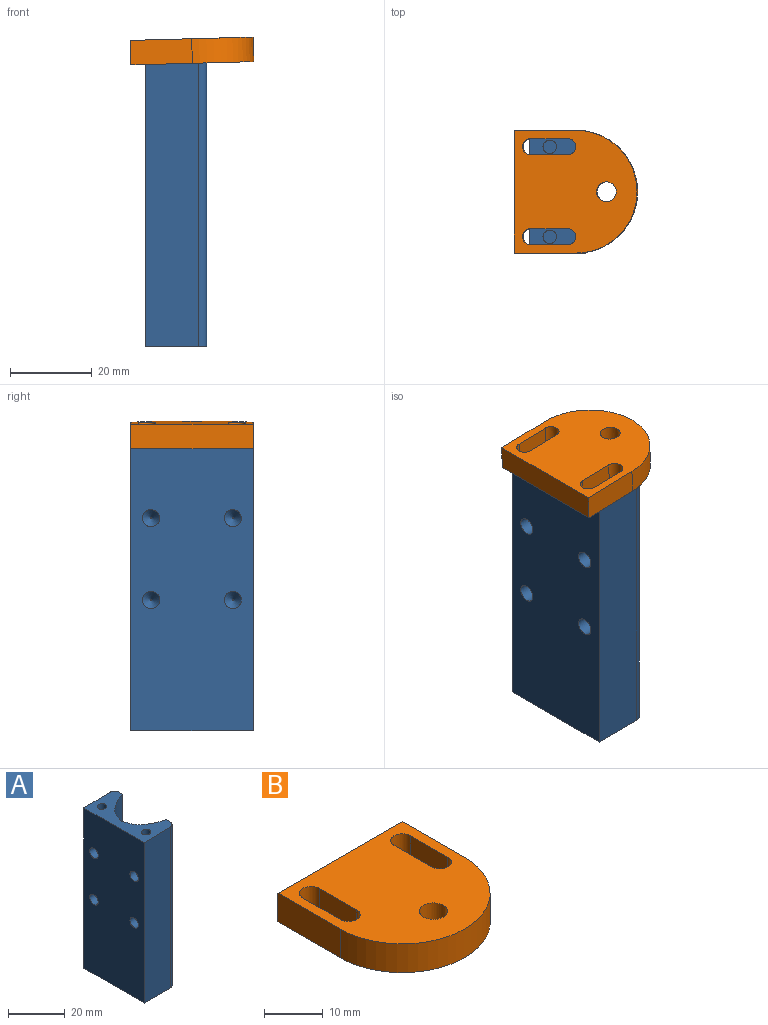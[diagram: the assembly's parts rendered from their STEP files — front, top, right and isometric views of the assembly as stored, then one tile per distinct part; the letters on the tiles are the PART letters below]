
ASSEMBLY  parts=2 mates=1
PART A: 31 faces, bbox 15x30x69.4 mm
  f0: cylinder r=9mm len=69.2mm, axis (0,0,-1), area 308mm2, adj f1,f3,f24,f29,f30
  f1: plane 30x15mm, normal (0,0,-1), area 300.9mm2, adj f0,f2,f3,f4,f5,f6,f7,f8
  f2: plane 69.35x13mm, normal (0,1,0), area 899.3mm2, adj f1,f9,f11,f24
  f3: cylinder r=20.05mm len=69.41mm, axis (0,0,-1), area 603.1mm2, adj f0,f1,f4,f24
  f4: plane 69.41x2.13mm, normal (1,0,0), area 148.1mm2, adj f1,f3,f9,f24
  f5: plane 69.35x13mm, normal (0,-1,0), area 899.3mm2, adj f1,f10,f11,f24
  f6: plane 69.41x2.13mm, normal (1,0,0), area 148.1mm2, adj f1,f7,f10,f24
  f7: cylinder r=20.05mm len=69.41mm, axis (0,0,-1), area 603.1mm2, adj f1,f6,f8,f24
  f8: cylinder r=9mm len=69.2mm, axis (0,0,-1), area 308mm2, adj f1,f7,f24,f29,f30
  f9: cylinder r=2mm len=69.41mm, axis (0,0,-1), area 218mm2, adj f1,f2,f4,f24
  f10: cylinder r=2mm len=69.41mm, axis (0,0,1), area 218mm2, adj f1,f5,f6,f24
  f11: plane 69x30mm, normal (-1,0,0), area 2014.6mm2, adj f1,f2,f5,f12,f14,f16,f18,f24
  f12: cylinder r=2.1mm len=6.5mm, axis (-1,0,0), area 85.8mm2, adj f11,f21
  f13: plane 0.2x0.2mm, normal (-1,0,0), area 0mm2, adj f21
  f14: cylinder r=2.1mm len=6.5mm, axis (-1,0,0), area 85.8mm2, adj f11,f20
  f15: plane 0.2x0.2mm, normal (-1,0,0), area 0mm2, adj f20
  f16: cylinder r=2.1mm len=6.5mm, axis (-1,0,0), area 85.8mm2, adj f11,f22
  f17: plane 0.2x0.2mm, normal (-1,0,0), area 0mm2, adj f22
  f18: cylinder r=2.1mm len=6.5mm, axis (-1,0,0), area 85.8mm2, adj f11,f23
  f19: plane 0.2x0.2mm, normal (-1,0,0), area 0mm2, adj f23
  f20: cone r=0.1mm half-angle=45deg, axis (-1,0,0), area 19.5mm2, adj f14,f15
  f21: cone r=0.1mm half-angle=45deg, axis (-1,0,0), area 19.5mm2, adj f12,f13
  f22: cone r=0.1mm half-angle=45deg, axis (-1,0,0), area 19.5mm2, adj f16,f17
  f23: cone r=0.1mm half-angle=45deg, axis (-1,0,0), area 19.5mm2, adj f18,f19
  f24: plane 30.01x15.01mm, normal (-0.03,0,1), area 255.4mm2, adj f0,f2,f3,f4,f5,f6,f7,f8
  f25: plane 3.3x3.3mm, normal (0,0,1), area 8.6mm2, adj f26
  f26: cylinder r=1.65mm len=14.18mm, axis (0,0,1), area 146.5mm2, adj f24,f25
  f27: plane 3.3x3.3mm, normal (0,0,1), area 8.6mm2, adj f28
  f28: cylinder r=1.65mm len=14.18mm, axis (0,0,1), area 146.5mm2, adj f24,f27
  f29: cylinder r=2.5mm len=33.11mm, axis (0,0,-1), area 102.3mm2, adj f0,f8,f24,f30
  f30: plane 44.5x13.35mm, normal (1,0,0.08), area 367.8mm2, adj f0,f1,f8,f29
PART B: 15 faces, bbox 30x30x6 mm
  f0: plane 15x6mm, normal (1,0,0), area 90mm2, adj f1,f12,f13,f14
  f1: plane 30x6mm, normal (0,1,0), area 180mm2, adj f0,f11,f12,f13
  f2: cylinder r=2mm len=6mm, axis (0,0,-1), area 37.7mm2, adj f3,f8,f12,f13
  f3: plane 9x6mm, normal (-1,0,0), area 54mm2, adj f2,f4,f12,f13
  f4: cylinder r=2mm len=6mm, axis (0,0,-1), area 37.7mm2, adj f3,f8,f12,f13
  f5: cylinder r=2mm len=6mm, axis (0,0,-1), area 37.7mm2, adj f6,f9,f12,f13
  f6: plane 9x6mm, normal (-1,0,0), area 54mm2, adj f5,f7,f12,f13
  f7: cylinder r=2mm len=6mm, axis (0,0,-1), area 37.7mm2, adj f6,f9,f12,f13
  f8: plane 9x6mm, normal (1,0,0), area 54mm2, adj f2,f4,f12,f13
  f9: plane 9x6mm, normal (1,0,0), area 54mm2, adj f5,f7,f12,f13
  f10: cylinder r=2.42mm len=6mm, axis (0,0,-1), area 91.1mm2, adj f12,f13
  f11: plane 15x6mm, normal (-1,0,0), area 90mm2, adj f1,f12,f13,f14
  f12: plane 30x30mm, normal (0,0,1), area 688mm2, adj f0,f1,f2,f3,f4,f5,f6,f7
  f13: plane 30x30mm, normal (0,0,-1), area 688mm2, adj f0,f1,f2,f3,f4,f5,f6,f7
  f14: cylinder r=15mm len=30mm, axis (0,0,-1), area 282.7mm2, adj f0,f11,f12,f13
PLACE A t=(-12.38,4.88,-5.83)mm
PLACE B rot(axis=(-0.01,-0.01,1),90deg) t=(-20.88,4.88,63.48)mm
MATE fastened B.f13 <-> A.f24  axis (0.03,0,-1) through (-27.38,-6.12,63.3)mm
